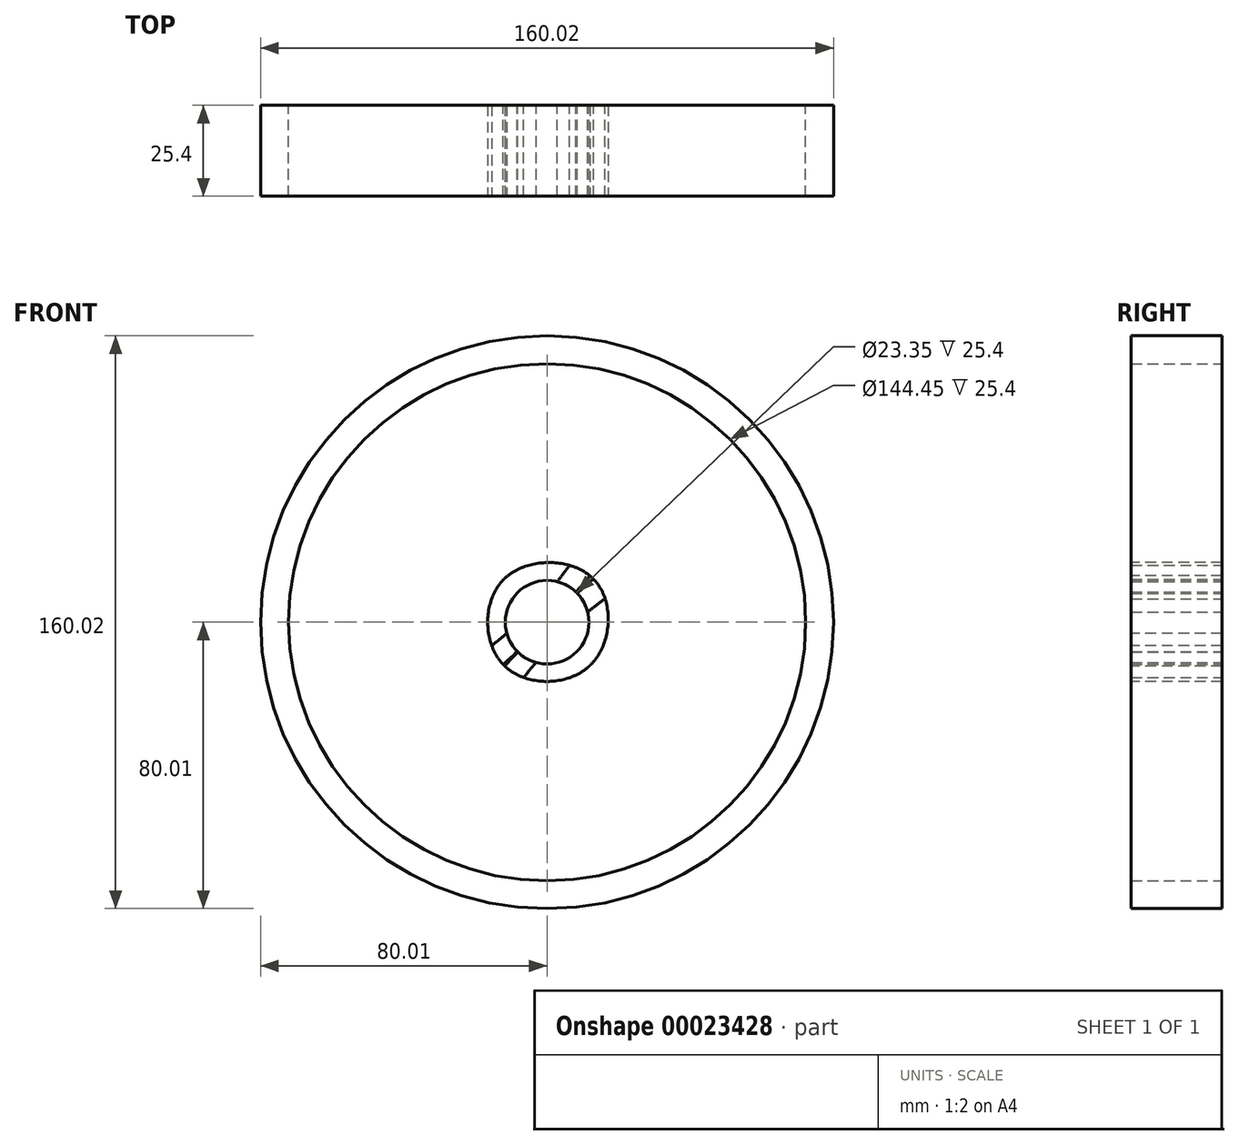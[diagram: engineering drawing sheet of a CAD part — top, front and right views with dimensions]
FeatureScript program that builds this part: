
annotation { "Feature Type Name" : "Feature", "Feature Type Description" : "" }
export const myFeature = defineFeature(function(context is Context, id is Id, definition is map)
    precondition{}
    {
        {
            var Q0;
            Q0=qCreatedBy(makeId("Front.planeOp"),FACE);
            var sketch = newSketch(context, id + "F0", { "sketchPlane" : qUnion([Q0])});
            skCircle(sketch, "E0", {"center": v(0, 0) * mm, "radius": 72.22 * mm});
            skFitSpline(sketch, "E1", {"points": [v(0, 0) * mm, v(-24.07, 36.11) * mm, v(0, 72.22) * mm], "startDerivative": vector(-72.22, 72.22) * mm, "endDerivative": vector(72.22, 72.22) * mm});
            skFitSpline(sketch, "E2", {"points": [v(0, 72.22) * mm, v(22.5, 36.11) * mm, v(0, 0) * mm], "startDerivative": vector(72.22, -72.22) * mm, "endDerivative": vector(-72.22, -72.22) * mm});
            skLineSegment(sketch, "E3", {"start": v(0, 0) * mm, "end": v(0, 0) * mm});
            skFitSpline(sketch, "E4", {"points": [v(-72.22, 0) * mm, v(-36.11, -24.07) * mm, v(0, 0) * mm], "startDerivative": vector(72.22, -72.22) * mm, "endDerivative": vector(72.22, 72.22) * mm});
            skFitSpline(sketch, "E5", {"points": [v(0, 0) * mm, v(-24.07, -36.11) * mm, v(0, -72.22) * mm], "startDerivative": vector(-72.22, -72.22) * mm, "endDerivative": vector(72.22, -72.22) * mm});
            skFitSpline(sketch, "E6", {"points": [v(0, -72.22) * mm, v(22.31, -36.11) * mm, v(0, 0) * mm], "startDerivative": vector(72.22, 72.22) * mm, "endDerivative": vector(-72.22, 72.22) * mm});
            skFitSpline(sketch, "E7", {"points": [v(0, 0) * mm, v(36.11, 22.79) * mm, v(72.22, 0) * mm], "startDerivative": vector(72.22, 72.22) * mm, "endDerivative": vector(72.22, -72.22) * mm});
            skFitSpline(sketch, "E8", {"points": [v(72.22, 0) * mm, v(36.11, -24.07) * mm, v(0, 0) * mm], "startDerivative": vector(-72.22, -72.22) * mm, "endDerivative": vector(-72.22, 72.22) * mm});
            skFitSpline(sketch, "E9", {"points": [v(-64.54, 0) * mm, v(-36.11, 17.39) * mm, v(-7.68, 0) * mm], "startDerivative": vector(56.86, 52.16) * mm, "endDerivative": vector(56.86, -52.16) * mm});
            skFitSpline(sketch, "E10", {"points": [v(-7.68, 0) * mm, v(-36.11, -16.4) * mm, v(-64.54, 0) * mm], "startDerivative": vector(-56.86, -49.18) * mm, "endDerivative": vector(-56.86, 49.18) * mm});
            skFitSpline(sketch, "E11", {"points": [v(0, 64.54) * mm, v(-16.4, 36.11) * mm, v(0, 7.68) * mm], "startDerivative": vector(-49.18, -56.86) * mm, "endDerivative": vector(49.18, -56.86) * mm});
            skFitSpline(sketch, "E12", {"points": [v(0, 7.68) * mm, v(14.82, 36.11) * mm, v(0, 64.54) * mm], "startDerivative": vector(44.46, 56.86) * mm, "endDerivative": vector(-44.46, 56.86) * mm});
            skFitSpline(sketch, "E13", {"points": [v(0, -7.68) * mm, v(-16.4, -36.11) * mm, v(0, -64.54) * mm], "startDerivative": vector(-49.18, -56.86) * mm, "endDerivative": vector(49.18, -56.86) * mm});
            skFitSpline(sketch, "E14", {"points": [v(0, -64.54) * mm, v(14.63, -36.11) * mm, v(0, -7.68) * mm], "startDerivative": vector(43.9, 56.86) * mm, "endDerivative": vector(-43.9, 56.86) * mm});
            skFitSpline(sketch, "E15", {"points": [v(7.68, 0) * mm, v(36.11, -16.4) * mm, v(64.54, 0) * mm], "startDerivative": vector(56.86, -49.18) * mm, "endDerivative": vector(56.86, 49.18) * mm});
            skFitSpline(sketch, "E16", {"points": [v(64.54, 0) * mm, v(36.11, 15.1) * mm, v(7.68, 0) * mm], "startDerivative": vector(-56.86, 45.32) * mm, "endDerivative": vector(-56.86, -45.32) * mm});
            skCircle(sketch, "E17", {"center": v(0, 0) * mm, "radius": 80.01 * mm});
            skFitSpline(sketch, "E18", {"points": [v(-12.04, -12.04) * mm, v(-12.04, 12.04) * mm, v(12.97, 12.04) * mm, v(12.04, -12.04) * mm, v(-12.04, -12.04) * mm]});
            skFitSpline(sketch, "E19.trimOffspring", {"points": [v(0, 0) * mm, v(-36.11, 25.07) * mm, v(-72.22, 0) * mm], "startDerivative": vector(-72.22, 72.22) * mm, "endDerivative": vector(-72.22, -72.22) * mm});
            skCircle(sketch, "E20", {"center": v(0, 0) * mm, "radius": 11.67 * mm});
            skSolve(sketch);
        }
        {
            var Q0;
            Q0=makeQuery(id+"F0.imprint","IMPRINT",FACE,{"disambiguationData":[TD([[makeQuery(id+"F0.imprint","IMPRINT",EDGE,{"derivedFrom":sQuery(id+"F0.wireOp",EDGE,"E17")}),1.0]])]});
            extrude(context, id + "F1", {"entities" : qUnion([Q0]), "depth" : 25.4 * mm});
        }
        {
            var Q0;
            {var subQ0=sQuery(id+"F0.wireOp",EDGE,"E4");Q0=makeQuery(id+"F0.imprint","IMPRINT",FACE,{"disambiguationData":[TD([[makeQuery(id+"F0.imprint","IMPRINT",EDGE,{"derivedFrom":subQ0}),1.0]])]});}
            extrude(context, id + "F2", {"entities" : qUnion([Q0]), "depth" : 25.4 * mm});
        }
        {
            var Q0;
            {var subQ3=sQuery(id+"F0.wireOp",EDGE,"E2");Q0=makeQuery(id+"F0.imprint","IMPRINT",FACE,{"disambiguationData":[TD([[makeQuery(id+"F0.imprint","IMPRINT",EDGE,{"derivedFrom":subQ3}),-1.0]])]});}
            extrude(context, id + "F3", {"entities" : qUnion([Q0]), "depth" : 25.4 * mm});
        }
        {
            var Q0;
            Q0=makeQuery(id+"F0.imprint","IMPRINT",FACE,{"disambiguationData":[TD([[makeQuery(id+"F0.imprint","IMPRINT",EDGE,{"derivedFrom":sQuery(id+"F0.wireOp",EDGE,"E7")}),-1.0]])]});
            extrude(context, id + "F4", {"entities" : qUnion([Q0]), "depth" : 25.4 * mm});
        }
        {
            var Q0;
            Q0=makeQuery(id+"F0.imprint","IMPRINT",FACE,{"disambiguationData":[TD([[makeQuery(id+"F0.imprint","IMPRINT",EDGE,{"derivedFrom":sQuery(id+"F0.wireOp",EDGE,"E5")}),1.0]])]});
            extrude(context, id + "F5", {"entities" : qUnion([Q0]), "depth" : 25.4 * mm});
        }
        {
            var Q0;
            Q0=makeQuery(id+"F0.imprint","IMPRINT",FACE,{"disambiguationData":[TD([[makeQuery(id+"F0.imprint","IMPRINT",EDGE,{"derivedFrom":sQuery(id+"F0.wireOp",EDGE,"E20")}),-1.0]])]});
            extrude(context, id + "F6", {"entities" : qUnion([Q0]), "depth" : 25.4 * mm});
        }
    });
